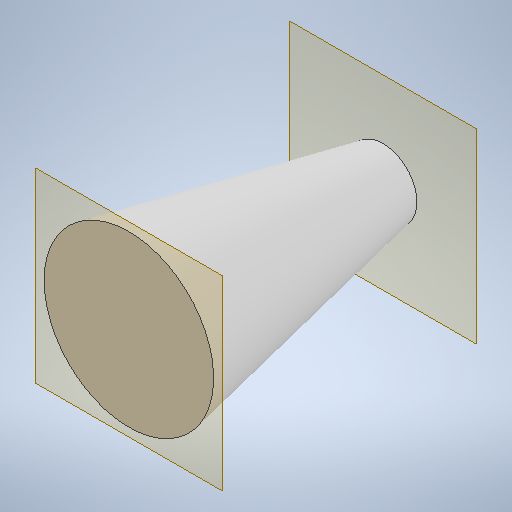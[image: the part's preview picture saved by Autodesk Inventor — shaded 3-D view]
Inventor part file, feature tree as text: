
AUTODESK INVENTOR PART (.ipt)
format: ipt  version: 2025.2 (Build 292293000, 293)  size: 232,960 bytes
history: native  units: mm
features: other x2, sketch x2, loft x1
ambient origin geometry x8: Origin, YZ Plane, XZ Plane, XY Plane, X Axis, Y Axis, Z Axis, Center Point
bodies: Body1 (feature_tree)
feature tree (5):
  other  "Sólido1"
  other  "Plano de trabalho1"
  loft  "Transição1"
  sketch  "Esboço1"  dims[d0=20.0mm d1=-30.0mm]
  sketch  "Esboço2"  dims[d2=8.0mm d3=0.0mm d4=90.0deg d5=0.0mm d6=90.0deg]
